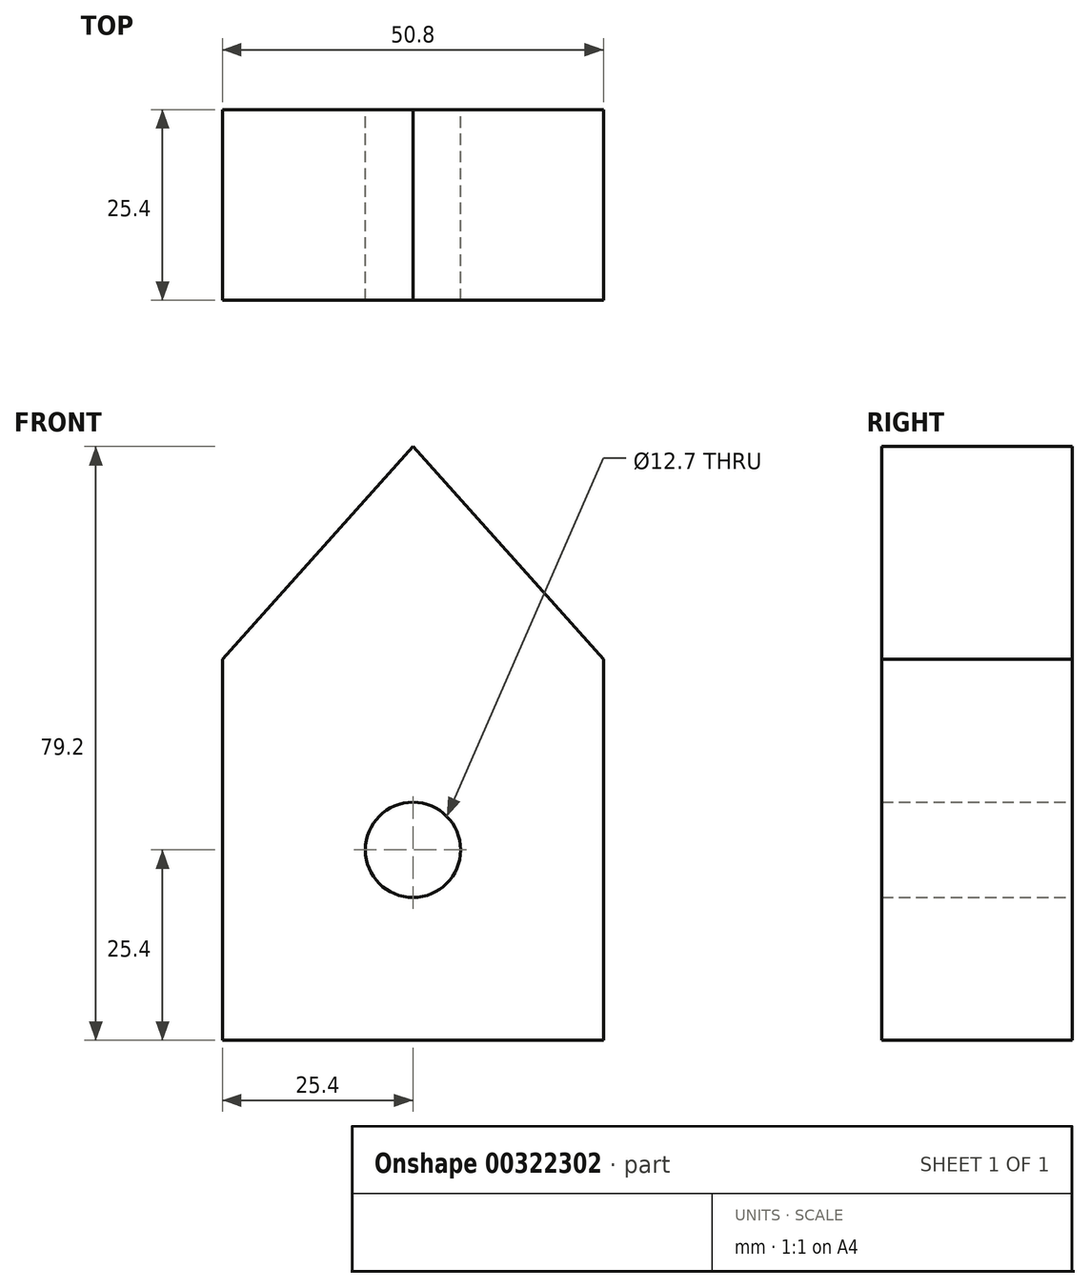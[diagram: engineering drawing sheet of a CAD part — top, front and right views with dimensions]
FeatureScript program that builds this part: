
annotation { "Feature Type Name" : "Feature", "Feature Type Description" : "" }
export const myFeature = defineFeature(function(context is Context, id is Id, definition is map)
    precondition{}
    {
        {
            var Q0;
            Q0=qCreatedBy(makeId("Front.planeOp"),FACE);
            var sketch = newSketch(context, id + "F0", { "sketchPlane" : qUnion([Q0])});
            skLineSegment(sketch, "E0.bottom", {"start": v(-25.4, -25.4) * mm, "end": v(25.4, -25.4) * mm});
            skLineSegment(sketch, "E0.top", {"start": v(-25.4, 25.4) * mm, "end": v(25.4, 25.4) * mm});
            skLineSegment(sketch, "E0.left", {"start": v(-25.4, -25.4) * mm, "end": v(-25.4, 25.4) * mm});
            skLineSegment(sketch, "E0.right", {"start": v(25.4, -25.4) * mm, "end": v(25.4, 25.4) * mm});
            skPoint(sketch, "E0.middle", {"position": v(0, 0) * mm});
            skLineSegment(sketch, "E1", {"start": v(-25.4, 25.4) * mm, "end": v(0, 53.8) * mm});
            skLineSegment(sketch, "E2", {"start": v(25.4, 25.4) * mm, "end": v(0, 53.8) * mm});
            skLineSegment(sketch, "E3.0", {"start": v(-25.4, -6.35) * mm, "end": v(-6.35, -6.35) * mm});
            skLineSegment(sketch, "E4.0", {"start": v(-6.35, -25.4) * mm, "end": v(-6.35, -6.35) * mm});
            skCircle(sketch, "E5", {"center": v(0, 0) * mm, "radius": 6.35 * mm});
            skSolve(sketch);
        }
        {
            var Q0;
            Q0 = qSketchRegion(id + "F0", true);
            extrude(context, id + "F1", {"entities" : qUnion([Q0]), "depth" : 25.4 * mm});
        }
    });
